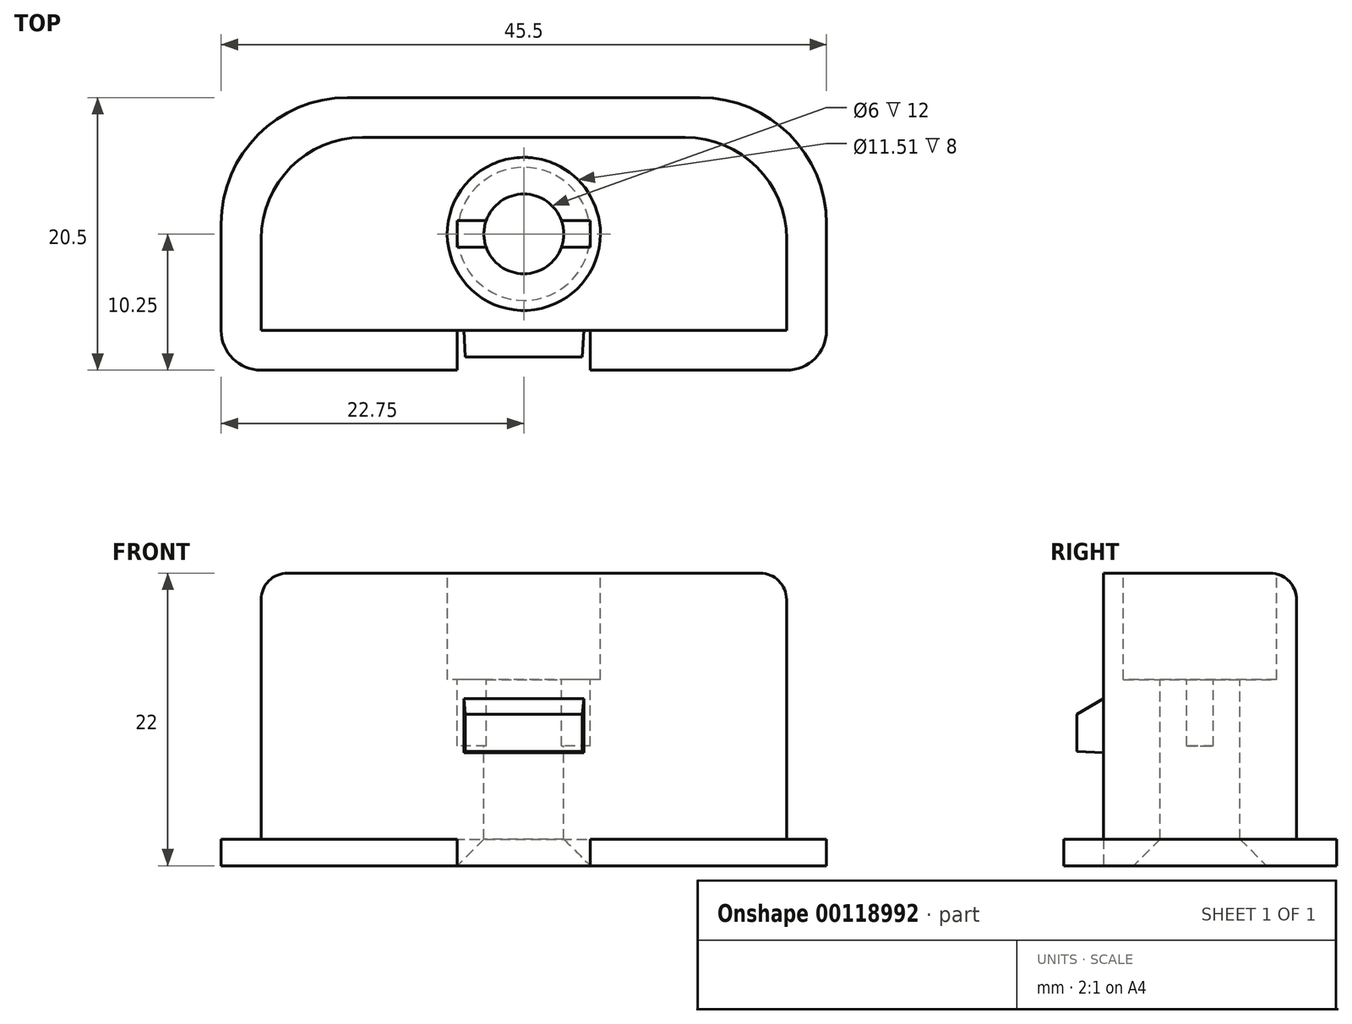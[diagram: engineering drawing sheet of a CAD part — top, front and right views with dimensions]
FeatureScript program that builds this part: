
annotation { "Feature Type Name" : "Feature", "Feature Type Description" : "" }
export const myFeature = defineFeature(function(context is Context, id is Id, definition is map)
    precondition{}
    {
        {
            var Q0;
            Q0=qCreatedBy(makeId("Top.planeOp"),FACE);
            var sketch = newSketch(context, id + "F0", { "sketchPlane" : qUnion([Q0])});
            skLineSegment(sketch, "E0.bottom", {"start": v(7.62, 0) * mm, "end": v(31.88, 0) * mm});
            skLineSegment(sketch, "E0.top", {"start": v(0, -14.5) * mm, "end": v(39.5, -14.5) * mm});
            skLineSegment(sketch, "E0.left", {"start": v(0, -7.62) * mm, "end": v(0, -14.5) * mm});
            skLineSegment(sketch, "E0.right", {"start": v(39.5, -7.62) * mm, "end": v(39.5, -14.5) * mm});
            skPoint(sketch, "E1.visualSharp", {"position": v(39.5, 0) * mm});
            skArc(sketch, "E1.filletArc", {"start": v(39.5, -7.62) * mm, "mid": v(37.27, -2.23) * mm, "end": v(31.88, 0) * mm});
            skPoint(sketch, "E2.visualSharp", {"position": v(0, 0) * mm});
            skArc(sketch, "E2.filletArc", {"start": v(7.62, 0) * mm, "mid": v(2.23, -2.23) * mm, "end": v(0, -7.62) * mm});
            skLineSegment(sketch, "E3", {"start": v(19.75, -14.5) * mm, "end": v(19.75, 0) * mm, "construction": true});
            skSolve(sketch);
        }
        {
            var Q0;
            Q0=makeQuery(id+"F0.imprint","IMPRINT",FACE,{"disambiguationData":[TD([[makeQuery(id+"F0.imprint","IMPRINT",EDGE,{"derivedFrom":sQuery(id+"F0.wireOp",EDGE,"E0.bottom")}),-1.0]])]});
            extrude(context, id + "F1", {"entities" : qUnion([Q0]), "depth" : 20 * mm});
        }
        {
            var Q0;
            Q0=makeQuery(id+"F1.opExtrude","CAP_FACE",FACE,{"disambiguationData":[OSD([sQuery(id+"F0.wireOp",EDGE,"E0.bottom"),sQuery(id+"F0.wireOp",EDGE,"E0.top"),sQuery(id+"F0.wireOp",EDGE,"E0.left"),sQuery(id+"F0.wireOp",EDGE,"E0.right"),sQuery(id+"F0.wireOp",EDGE,"E1.filletArc"),sQuery(id+"F0.wireOp",EDGE,"E2.filletArc")])],"isStart":false});
            var sketch = newSketch(context, id + "F2", { "sketchPlane" : qUnion([Q0])});
            skSolve(sketch);
        }
        {
            var Q0;
            Q0=makeQuery(id+"F1.opExtrude","CAP_FACE",FACE,{"disambiguationData":[OSD([sQuery(id+"F0.wireOp",EDGE,"E0.bottom"),sQuery(id+"F0.wireOp",EDGE,"E0.top"),sQuery(id+"F0.wireOp",EDGE,"E0.left"),sQuery(id+"F0.wireOp",EDGE,"E0.right"),sQuery(id+"F0.wireOp",EDGE,"E1.filletArc"),sQuery(id+"F0.wireOp",EDGE,"E2.filletArc")])],"isStart":true});
            var sketch = newSketch(context, id + "F3", { "sketchPlane" : qUnion([Q0])});
            skLineSegment(sketch, "E4.bottom", {"start": v(-3, 17.5) * mm, "end": v(42.5, 17.5) * mm});
            skLineSegment(sketch, "E4.top", {"start": v(6.5, -3) * mm, "end": v(33, -3) * mm});
            skLineSegment(sketch, "E4.left", {"start": v(-3, 17.5) * mm, "end": v(-3, 6.5) * mm});
            skLineSegment(sketch, "E4.right", {"start": v(42.5, 17.5) * mm, "end": v(42.5, 6.5) * mm});
            skPoint(sketch, "E5.visualSharp", {"position": v(-3, -3) * mm});
            skArc(sketch, "E5.filletArc", {"start": v(-3, 6.5) * mm, "mid": v(-0.22, -0.22) * mm, "end": v(6.5, -3) * mm});
            skPoint(sketch, "E6.visualSharp", {"position": v(42.5, -3) * mm});
            skArc(sketch, "E6.filletArc", {"start": v(33, -3) * mm, "mid": v(39.72, -0.22) * mm, "end": v(42.5, 6.5) * mm});
            skLineSegment(sketch, "E7", {"start": v(0, 14.5) * mm, "end": v(-3, 14.5) * mm, "construction": true});
            skLineSegment(sketch, "E8", {"start": v(0, 14.5) * mm, "end": v(0, 17.5) * mm, "construction": true});
            skLineSegment(sketch, "E9", {"start": v(39.5, 14.5) * mm, "end": v(42.5, 14.5) * mm, "construction": true});
            skLineSegment(sketch, "E10", {"start": v(19.75, 0) * mm, "end": v(19.75, -3) * mm, "construction": true});
            skSolve(sketch);
        }
        {
            var Q0;
            Q0=qSketchRegion(id+"F3",true);
            extrude(context, id + "F4", {"entities" : qUnion([Q0]), "operationType" : NewBodyOperationType.ADD, "depth" : 2 * mm});
        }
        {
            var Q0;
            Q0=makeQuery(id+"F4.opExtrude","CAP_FACE",FACE,{"disambiguationData":[OSD([sQuery(id+"F3.wireOp",EDGE,"E4.bottom"),sQuery(id+"F3.wireOp",EDGE,"E4.top"),sQuery(id+"F3.wireOp",EDGE,"E4.left"),sQuery(id+"F3.wireOp",EDGE,"E4.right"),sQuery(id+"F3.wireOp",EDGE,"E5.filletArc"),sQuery(id+"F3.wireOp",EDGE,"E6.filletArc")])],"isStart":false});
            var sketch = newSketch(context, id + "F5", { "sketchPlane" : qUnion([Q0])});
            skLineSegment(sketch, "E11", {"start": v(19.75, -3) * mm, "end": v(19.75, 17.5) * mm, "construction": true});
            skCircle(sketch, "E12", {"center": v(19.75, 7.25) * mm, "radius": 1.34 * mm});
            skSolve(sketch);
        }
        {
            var Q0;
            Q0=sQuery(id+"F5.wireOp",VERTEX,"E12.center");
            var Q1;
            Q1=makeQuery(id+"F1.opExtrude","SWEPT_BODY",BODY,{"disambiguationData":[OSD([sQuery(id+"F0.wireOp",EDGE,"E0.bottom"),sQuery(id+"F0.wireOp",EDGE,"E0.top"),sQuery(id+"F0.wireOp",EDGE,"E0.left"),sQuery(id+"F0.wireOp",EDGE,"E0.right"),sQuery(id+"F0.wireOp",EDGE,"E1.filletArc"),sQuery(id+"F0.wireOp",EDGE,"E2.filletArc")])]});
            hole(context, id + "F6", {"style" : HoleStyle.C_SINK, "endStyle" : HoleEndStyle.BLIND, "holeDiameter" : 6 * mm, "cSinkDiameter" : 10 * mm, "cSinkAngle" : 90 * degree, "holeDepth" : 25 * mm, "locations" : qUnion([Q0]), "scope" : qUnion([Q1]), "startStyle" : HoleStartStyle.SKETCH});
        }
        {
            var Q0;
            Q0=makeQuery(id+"F1.opExtrude","SWEPT_FACE",FACE,{"disambiguationData":[OSD([sQuery(id+"F0.wireOp",EDGE,"E0.top")])]});
            var sketch = newSketch(context, id + "F7", { "sketchPlane" : qUnion([Q0])});
            skLineSegment(sketch, "E13", {"start": v(19.75, 0) * mm, "end": v(19.75, 6.5) * mm, "construction": true});
            skLineSegment(sketch, "E14", {"start": v(19.75, 6.5) * mm, "end": v(15.25, 6.5) * mm, "construction": true});
            skLineSegment(sketch, "E15", {"start": v(15.25, 6.5) * mm, "end": v(24.25, 6.5) * mm, "construction": true});
            skLineSegment(sketch, "E16.bottom", {"start": v(15.25, 6.5) * mm, "end": v(24.25, 6.5) * mm});
            skLineSegment(sketch, "E16.top", {"start": v(15.25, 6.5) * mm, "end": v(24.25, 6.5) * mm});
            skLineSegment(sketch, "E16.left", {"start": v(15.25, 6.5) * mm, "end": v(15.25, 6.5) * mm});
            skLineSegment(sketch, "E16.right", {"start": v(24.25, 6.5) * mm, "end": v(24.25, 6.5) * mm});
            skLineSegment(sketch, "E17.top", {"start": v(15.25, 11.5) * mm, "end": v(24.25, 11.5) * mm});
            skLineSegment(sketch, "E17.left", {"start": v(15.25, 6.5) * mm, "end": v(15.25, 11.5) * mm});
            skLineSegment(sketch, "E17.right", {"start": v(24.25, 6.5) * mm, "end": v(24.25, 11.5) * mm});
            skSolve(sketch);
        }
        {
            var Q0;
            Q0 = qSketchRegion(id + "F7", true);
            extrude(context, id + "F8", {"entities" : qUnion([Q0]), "operationType" : NewBodyOperationType.ADD, "depth" : 2 * mm, "hasDraft" : true, "draftAngle" : 3 * degree, "draftPullDirection" : true});
        }
        {
            var Q0;
            Q0=makeQuery(id+"F8.opExtrude","CAP_EDGE",EDGE,{"disambiguationData":[OSD([sQuery(id+"F7.wireOp",EDGE,"E17.top")])],"isStart":false});
            chamfer(context, id + "F9", {"entities" : qUnion([Q0]), "chamferType" : ChamferType.OFFSET_ANGLE, "width" : 2 * mm, "oppositeDirection" : false, "angle" : 60 * degree, "tangentPropagation" : true});
        }
        {
            var Q0;
            Q0=makeQuery(id+"F4.opExtrude","CAP_FACE",FACE,{"disambiguationData":[OSD([sQuery(id+"F3.wireOp",EDGE,"E4.bottom"),sQuery(id+"F3.wireOp",EDGE,"E4.top"),sQuery(id+"F3.wireOp",EDGE,"E4.left"),sQuery(id+"F3.wireOp",EDGE,"E4.right"),sQuery(id+"F3.wireOp",EDGE,"E5.filletArc"),sQuery(id+"F3.wireOp",EDGE,"E6.filletArc")])],"isStart":false});
            var sketch = newSketch(context, id + "F10", { "sketchPlane" : qUnion([Q0])});
            skLineSegment(sketch, "E18.bottom", {"start": v(24.75, 14.5) * mm, "end": v(14.75, 14.5) * mm});
            skLineSegment(sketch, "E18.top", {"start": v(24.75, 20.5) * mm, "end": v(14.75, 20.5) * mm});
            skLineSegment(sketch, "E18.left", {"start": v(24.75, 14.5) * mm, "end": v(24.75, 20.5) * mm});
            skLineSegment(sketch, "E18.right", {"start": v(14.75, 14.5) * mm, "end": v(14.75, 20.5) * mm});
            skPoint(sketch, "E18.middle", {"position": v(19.75, 17.5) * mm});
            skSolve(sketch);
        }
        {
            var Q0;
            Q0 = qSketchRegion(id + "F10", true);
            extrude(context, id + "F11", {"entities" : qUnion([Q0]), "operationType" : NewBodyOperationType.REMOVE, "oppositeDirection" : true, "depth" : 5 * mm});
        }
        {
            var Q0;
            Q0=makeQuery(id+"F2.imprint","IMPRINT",FACE,{"disambiguationData":[TD([[makeQuery(id+"F2.imprint","IMPRINT",EDGE,{"derivedFrom":makeQuery(id+"F1.opExtrude","CAP_EDGE",EDGE,{"disambiguationData":[OSD([sQuery(id+"F0.wireOp",EDGE,"E0.bottom")])],"isStart":false})}),-1.0]])]});
            var sketch = newSketch(context, id + "F12", { "sketchPlane" : qUnion([Q0])});
            skCircle(sketch, "E19", {"center": v(19.75, -7.25) * mm, "radius": 5.75 * mm});
            skSolve(sketch);
        }
        {
            var Q0;
            Q0 = qSketchRegion(id + "F12", true);
            extrude(context, id + "F13", {"entities" : qUnion([Q0]), "operationType" : NewBodyOperationType.REMOVE, "oppositeDirection" : true, "depth" : 8 * mm});
        }
        {
            var Q0;
            Q0=makeQuery(id+"F2.imprint","IMPRINT",FACE,{"disambiguationData":[TD([[makeQuery(id+"F2.imprint","IMPRINT",EDGE,{"derivedFrom":makeQuery(id+"F1.opExtrude","CAP_EDGE",EDGE,{"disambiguationData":[OSD([sQuery(id+"F0.wireOp",EDGE,"E0.bottom")])],"isStart":false})}),-1.0]])]});
            var sketch = newSketch(context, id + "F14", { "sketchPlane" : qUnion([Q0])});
            skLineSegment(sketch, "E20.bottom", {"start": v(24.75, -8.25) * mm, "end": v(14.75, -8.25) * mm});
            skLineSegment(sketch, "E20.top", {"start": v(24.75, -6.25) * mm, "end": v(14.75, -6.25) * mm});
            skLineSegment(sketch, "E20.left", {"start": v(24.75, -8.25) * mm, "end": v(24.75, -6.25) * mm});
            skLineSegment(sketch, "E20.right", {"start": v(14.75, -8.25) * mm, "end": v(14.75, -6.25) * mm});
            skPoint(sketch, "E20.middle", {"position": v(19.75, -7.25) * mm});
            skSolve(sketch);
        }
        {
            var Q0;
            Q0 = qSketchRegion(id + "F14", true);
            extrude(context, id + "F15", {"entities" : qUnion([Q0]), "operationType" : NewBodyOperationType.REMOVE, "oppositeDirection" : true, "depth" : 13 * mm});
        }
        {
            var Q0;
            Q0=makeQuery(id+"F1.opExtrude","CAP_EDGE",EDGE,{"disambiguationData":[OSD([sQuery(id+"F0.wireOp",EDGE,"E2.filletArc")])],"isStart":false});
            fillet(context, id + "F16", {"entities" : qUnion([Q0]), "radius" : 2 * mm, "tangentPropagation" : true, "allowEdgeOverflow" : false});
        }
        {
            var Q0;
            Q0=makeQuery(id+"F4.opExtrude","SWEPT_EDGE",EDGE,{"disambiguationData":[OSD([sQuery(id+"F3.wireOp",EDGE,"E4.bottom"),sQuery(id+"F3.wireOp",EDGE,"E4.right")])]});
            var Q1;
            Q1=makeQuery(id+"F4.opExtrude","SWEPT_EDGE",EDGE,{"disambiguationData":[OSD([sQuery(id+"F3.wireOp",EDGE,"E4.bottom"),sQuery(id+"F3.wireOp",EDGE,"E4.left")])]});
            fillet(context, id + "F17", {"entities" : qUnion([Q0, Q1]), "radius" : 3 * mm, "tangentPropagation" : true, "allowEdgeOverflow" : false});
        }
    });
